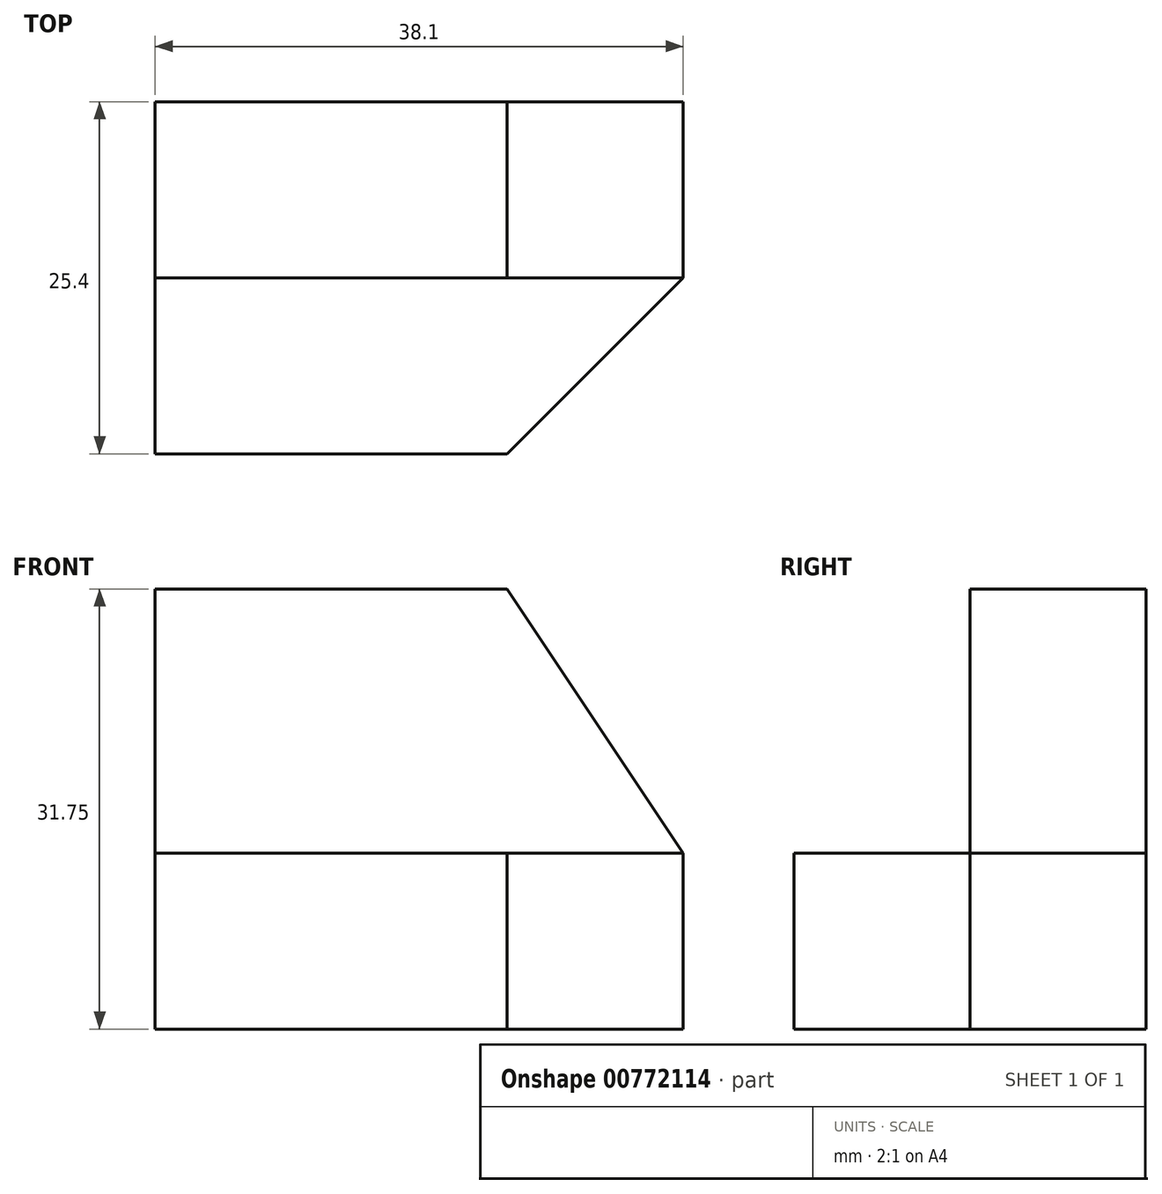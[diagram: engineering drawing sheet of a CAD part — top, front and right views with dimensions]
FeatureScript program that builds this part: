
annotation { "Feature Type Name" : "Feature", "Feature Type Description" : "" }
export const myFeature = defineFeature(function(context is Context, id is Id, definition is map)
    precondition{}
    {
        {
            var Q0;
            Q0=qCreatedBy(makeId("Front.planeOp"),FACE);
            var sketch = newSketch(context, id + "F0", { "sketchPlane" : qUnion([Q0])});
            skLineSegment(sketch, "E0", {"start": v(0, 0) * mm, "end": v(38.1, 0) * mm});
            skLineSegment(sketch, "E1", {"start": v(38.1, 0) * mm, "end": v(38.1, 31.75) * mm});
            skLineSegment(sketch, "E2", {"start": v(38.1, 31.75) * mm, "end": v(0, 31.75) * mm});
            skLineSegment(sketch, "E3", {"start": v(0, 31.75) * mm, "end": v(0, 0) * mm});
            skSolve(sketch);
        }
        {
            var Q0;
            Q0 = qSketchRegion(id + "F0", true);
            extrude(context, id + "F1", {"entities" : qUnion([Q0]), "depth" : 25.4 * mm, "offsetDistance" : 25.4 * mm});
        }
        {
            var Q0;
            Q0=makeQuery(id+"F1.opExtrude","CAP_FACE",FACE,{"disambiguationData":[OSD([sQuery(id+"F0.wireOp",EDGE,"E0"),sQuery(id+"F0.wireOp",EDGE,"E1"),sQuery(id+"F0.wireOp",EDGE,"E2"),sQuery(id+"F0.wireOp",EDGE,"E3")])],"isStart":false});
            var sketch = newSketch(context, id + "F2", { "sketchPlane" : qUnion([Q0])});
            skLineSegment(sketch, "E4", {"start": v(0, 0) * mm, "end": v(0, 12.7) * mm});
            skLineSegment(sketch, "E5", {"start": v(0, 12.7) * mm, "end": v(38.1, 12.7) * mm});
            skLineSegment(sketch, "E6", {"start": v(38.1, 12.7) * mm, "end": v(38.1, 0) * mm});
            skLineSegment(sketch, "E7", {"start": v(0, 0) * mm, "end": v(38.1, 0) * mm});
            skSolve(sketch);
        }
        {
            var Q0;
            {var subQ0=sQuery(id+"F2.wireOp",EDGE,"E5");Q0=makeQuery(id+"F2.imprint","IMPRINT",FACE,{"disambiguationData":[TD([[makeQuery(id+"F2.imprint","IMPRINT",EDGE,{"derivedFrom":subQ0}),1.0]])]});}
            extrude(context, id + "F3", {"entities" : qUnion([Q0]), "operationType" : NewBodyOperationType.REMOVE, "oppositeDirection" : true, "depth" : 12.7 * mm, "offsetDistance" : 25.4 * mm});
        }
        {
            var Q0;
            Q0=makeQuery(id+"F3.boolean.opBoolean","COPY",FACE,{"derivedFrom":makeQuery(id+"F3.opExtrude","CAP_FACE",FACE,{"disambiguationData":[OSD([sQuery(id+"F0.wireOp",EDGE,"E1"),sQuery(id+"F0.wireOp",EDGE,"E2"),sQuery(id+"F0.wireOp",EDGE,"E3"),sQuery(id+"F2.wireOp",EDGE,"E5")])],"isStart":false})});
            var sketch = newSketch(context, id + "F4", { "sketchPlane" : qUnion([Q0])});
            skLineSegment(sketch, "E8", {"start": v(0, 31.75) * mm, "end": v(25.4, 31.75) * mm});
            skLineSegment(sketch, "E9", {"start": v(25.4, 31.75) * mm, "end": v(38.1, 12.7) * mm});
            skSolve(sketch);
        }
        {
            var Q0;
            {var subQ0=sQuery(id+"F4.wireOp",EDGE,"E9");Q0=makeQuery(id+"F4.imprint","IMPRINT",FACE,{"disambiguationData":[TD([[makeQuery(id+"F4.imprint","IMPRINT",EDGE,{"derivedFrom":subQ0}),1.0]])]});}
            extrude(context, id + "F5", {"entities" : qUnion([Q0]), "operationType" : NewBodyOperationType.REMOVE, "oppositeDirection" : true, "depth" : 25.4 * mm, "offsetDistance" : 25.4 * mm});
        }
        {
            var Q0;
            Q0=makeQuery(id+"F1.opExtrude","SWEPT_FACE",FACE,{"disambiguationData":[OSD([sQuery(id+"F0.wireOp",EDGE,"E0")])]});
            var sketch = newSketch(context, id + "F6", { "sketchPlane" : qUnion([Q0])});
            skLineSegment(sketch, "E10", {"start": v(0, 25.4) * mm, "end": v(25.4, 25.4) * mm});
            skLineSegment(sketch, "E11", {"start": v(38.1, 0) * mm, "end": v(38.1, 12.7) * mm});
            skLineSegment(sketch, "E12", {"start": v(38.1, 12.7) * mm, "end": v(25.4, 25.4) * mm});
            skSolve(sketch);
        }
        {
            var Q0;
            {var subQ0=sQuery(id+"F6.wireOp",EDGE,"E12");Q0=makeQuery(id+"F6.imprint","IMPRINT",FACE,{"disambiguationData":[TD([[makeQuery(id+"F6.imprint","IMPRINT",EDGE,{"derivedFrom":subQ0}),-1.0]])]});}
            extrude(context, id + "F7", {"entities" : qUnion([Q0]), "operationType" : NewBodyOperationType.REMOVE, "oppositeDirection" : true, "depth" : 25.4 * mm, "offsetDistance" : 25.4 * mm});
        }
    });
